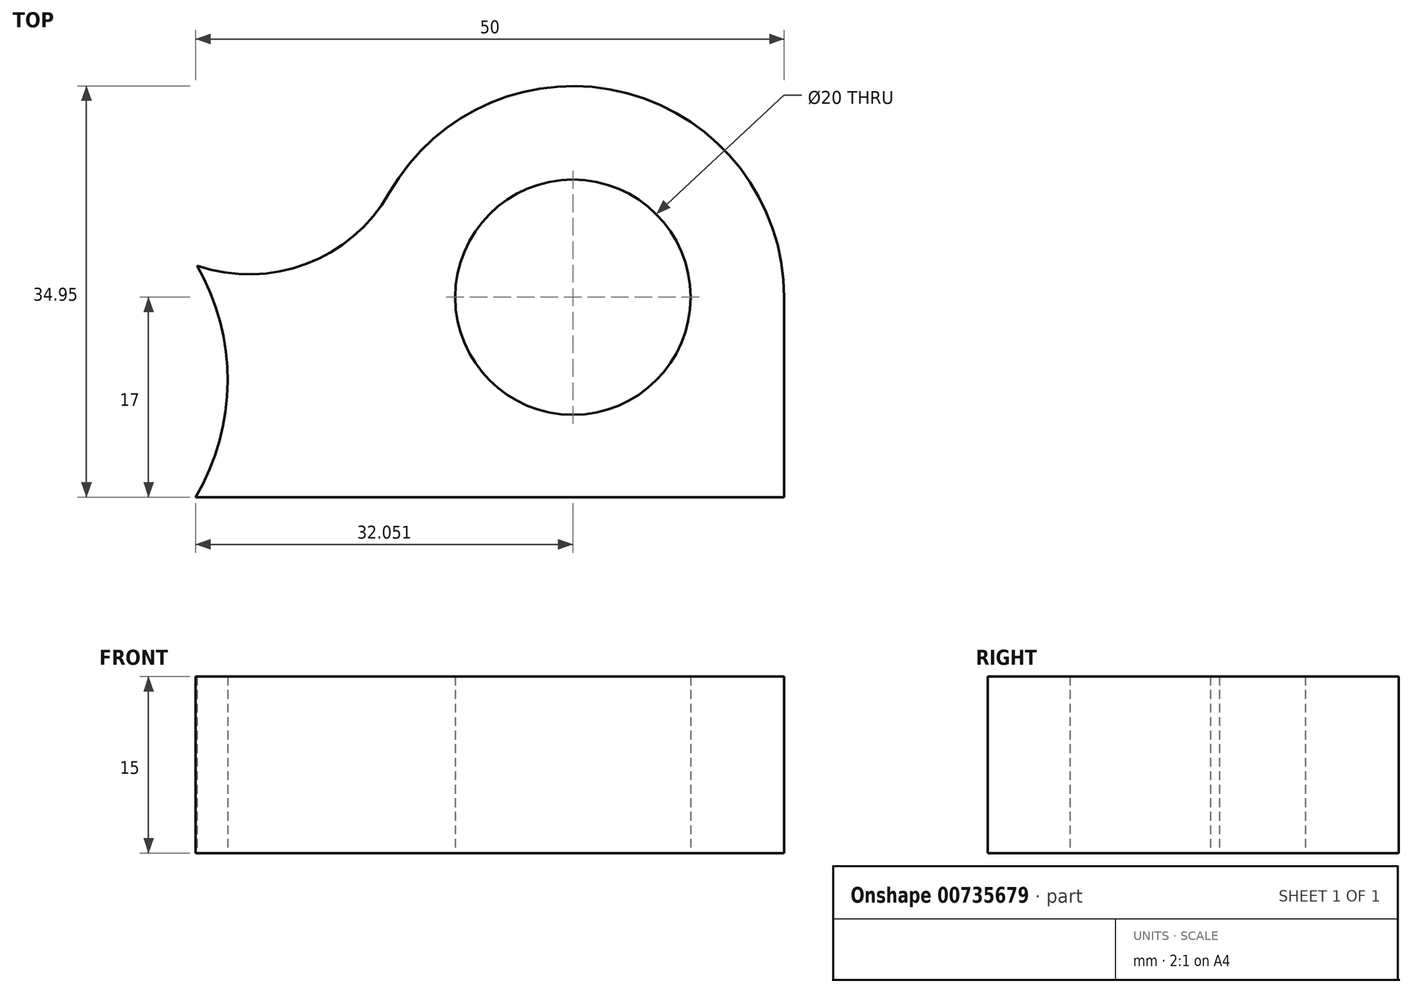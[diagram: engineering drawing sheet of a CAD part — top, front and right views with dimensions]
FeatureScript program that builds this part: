
annotation { "Feature Type Name" : "Feature", "Feature Type Description" : "" }
export const myFeature = defineFeature(function(context is Context, id is Id, definition is map)
    precondition{}
    {
        {
            var Q0;
            Q0=qCreatedBy(makeId("Top.planeOp"),FACE);
            var sketch = newSketch(context, id + "F0", { "sketchPlane" : qUnion([Q0])});
            skLineSegment(sketch, "E0", {"start": v(0, 0) * mm, "end": v(0, 17) * mm});
            skArc(sketch, "E1", {"start": v(0, 17) * mm, "mid": v(-13.36, 34.35) * mm, "end": v(-33.55, 25.87) * mm});
            skArc(sketch, "E2", {"start": v(-33.55, 25.87) * mm, "mid": v(-40.6, 19.83) * mm, "end": v(-49.88, 19.69) * mm});
            skLineSegment(sketch, "E3", {"start": v(0, 0) * mm, "end": v(-50, 0) * mm});
            skArc(sketch, "E4", {"start": v(-50, 0) * mm, "mid": v(-47.28, 9.83) * mm, "end": v(-49.88, 19.69) * mm});
            skCircle(sketch, "E5", {"center": v(-17.95, 17) * mm, "radius": 10 * mm});
            skSolve(sketch);
        }
        {
            var Q0;
            Q0 = qSketchRegion(id + "F0", true);
            extrude(context, id + "F1", {"entities" : qUnion([Q0]), "depth" : 15 * mm, "offsetDistance" : 25 * mm});
        }
    });
